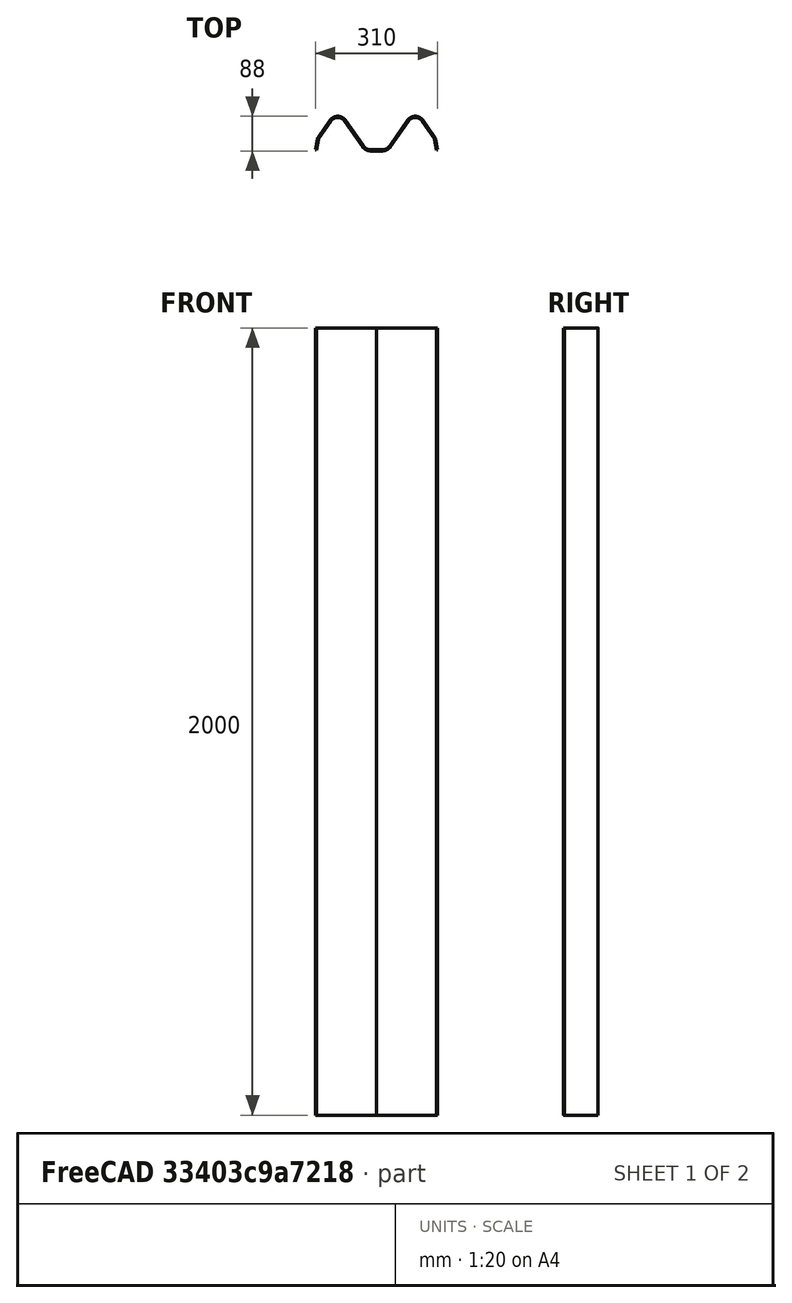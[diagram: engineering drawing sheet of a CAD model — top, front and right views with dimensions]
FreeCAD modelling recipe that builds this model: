
FCSTD DOCUMENT  (FreeCAD 0.21R33694 (Git))
Label: barrier
License: All rights reserved
LicenseURL: http://en.wikipedia.org/wiki/All_rights_reserved
objects: Sketcher::SketchObject×2, Fem::ConstraintFixed×2, Fem::ConstraintForce×2, Part::Offset2D×2, Fem::FemSolverObjectPython×1, App::MaterialObjectPython×1, Part::Mirroring×1, Part::FeaturePython×1, Part::Extrusion×1, Fem::FemMeshObjectPython×1, Fem::FemAnalysis×1
note: 7 computed .brp shape members not serialized (recipe doc carries the construction recipe); baked Part::Feature solids carry a one-line shape summary decoded from their .brp

FEATURE [Sketcher::SketchObject] Sketch
  FullyConstrained = false
  sketch-geometry (9):
    g0: LineSegment StartX=-155 StartY=0 StartZ=0 EndX=-150.163 EndY=27.4344 EndZ=0
    g1: ArcOfCircle CenterX=-140.315 CenterY=25.6979 CenterZ=0 NormalX=0 NormalY=0 NormalZ=1 AngleXU=0 Radius=10 StartAngle=2.53073 EndAngle=2.96706
    g2: LineSegment StartX=-148.506 StartY=31.4337 StartZ=0 EndX=-118.165 EndY=74.7658 EndZ=0
    g3: LineSegment StartX=0 StartY=0 StartZ=0 EndX=-14 EndY=0 EndZ=0
    g4: ArcOfCircle CenterX=-14 CenterY=24 CenterZ=0 NormalX=0 NormalY=0 NormalZ=1 AngleXU=0 Radius=24 StartAngle=3.75246 EndAngle=4.71239
    g5: LineSegment StartX=-33.6596 StartY=10.2342 StartZ=0 EndX=-78.8452 EndY=74.7658 EndZ=0
    g6: ArcOfCircle CenterX=-98.5049 CenterY=61 CenterZ=0 NormalX=0 NormalY=0 NormalZ=1 AngleXU=0 Radius=24 StartAngle=0.610865 EndAngle=2.53073
    g7: LineSegment StartX=-130.459 StartY=85 StartZ=0 EndX=-64.5536 EndY=85 EndZ=0
    g8: LineSegment StartX=-148.506 StartY=31.4337 StartZ=0 EndX=-148.506 EndY=74.2838 EndZ=0
  constraints (22):
    c: PointOnObject(g0,g-1)
    c: Angle(g0,g-2) = 0.174533
    c: Coincident(g3,g-1)
    c: PointOnObject(g3,g-1)
    c: Radius(g1) = 10
    c: DistanceX(g0,g3) = 155
    c: Radius(g4) = 24
    c: Angle(g-1,g5) = 2.18166
    c: DistanceX(g3,g3) = 14
    c: Horizontal(g7)
    c: DistanceY(g3,g7) = 85
    c: Tangent(g6,g7)
    c: Radius(g6) = 24
    c: Tangent(g6,g2) = 1.5708
    c: Tangent(g6,g5) = -1.5708
    c: Tangent(g1,g0) = 1.5708
    c: Tangent(g1,g2) = 1.5708
    c: Tangent(g4,g3) = 1.5708
    c: Tangent(g4,g5) = 1.5708
    c: Coincident(g8,g1)
    c: Vertical(g8)
    c: Angle(g2,g8) = 0.610865
FEATURE [Fem::ConstraintFixed] ConstraintFixed
  NormalDirection = (0,0,1)
FEATURE [Fem::ConstraintForce] ConstraintForce
  DirectionVector = (0.984808,-0.173648,0)
  Force = 15000
  NormalDirection = (-0.984808,0.173648,0)
  Reversed = true
FEATURE [Fem::FemSolverObjectPython] SolverCcxTools  # FEM object (typed FeaturePython)
  AnalysisType = 0
  BeamShellResultOutput3D = false
  BucklingFactors = 1
  EigenmodeHighLimit = 1000000
  EigenmodeLowLimit = 0
  EigenmodesCount = 10
  GeometricalNonlinearity = 0
  IterationsControlParameterCutb = 0.25,0.5,0.75,0.85,,,1.5,
  IterationsControlParameterIter = 4,8,9,200,10,400,,200,,
  IterationsControlParameterTimeUse = false
  IterationsThermoMechMaximum = 2000
  IterationsUserDefinedIncrementations = false
  IterationsUserDefinedTimeStepLength = false
  MaterialNonlinearity = 0
  MatrixSolverType = 0
  SplitInputWriter = false
  ThermoMechSteadyState = true
  TimeEnd = 1
  TimeInitialStep = 0.01
FEATURE [App::MaterialObjectPython] MaterialSolid  # material (typed FeaturePython)
  Category = 0
  Material = AuthorAndLicense=(c) 2014 M. Münch - GNU Lesser General Public License (LGPL),CardName=Steel-St-E-315,Density=7800 kg/m^3,Father=Metal,+13 more (map truncated)
FEATURE [Part::Offset2D] Offset2D
  Fill = true
  Intersection = false
  Join = 0
  Mode = 0
  SelfIntersection = false
  Source = -> Sketch
  Value = 3
FEATURE [Part::Mirroring] Part__Mirroring  label="Offset2D (Mirror #1)"
  Base = (0,0,0)
  Normal = (1,0,0)
  Source = -> Offset2D
FEATURE [Sketcher::SketchObject] Sketch001
  FullyConstrained = false
  sketch-geometry (8):
    g0: LineSegment StartX=-155 StartY=0 StartZ=0 EndX=-150.163 EndY=27.4344 EndZ=0
    g1: ArcOfCircle CenterX=-140.315 CenterY=25.6979 CenterZ=0 NormalX=0 NormalY=0 NormalZ=1 AngleXU=0 Radius=10 StartAngle=2.53073 EndAngle=2.96706
    g2: LineSegment StartX=-148.506 StartY=31.4337 StartZ=0 EndX=-118.165 EndY=74.7658 EndZ=0
    g3: LineSegment StartX=0 StartY=0 StartZ=0 EndX=-14 EndY=0 EndZ=0
    g4: ArcOfCircle CenterX=-14 CenterY=24 CenterZ=0 NormalX=0 NormalY=0 NormalZ=1 AngleXU=0 Radius=24 StartAngle=3.75246 EndAngle=4.71239
    g5: LineSegment StartX=-33.6596 StartY=10.2342 StartZ=0 EndX=-78.8452 EndY=74.7658 EndZ=0
    g6: ArcOfCircle CenterX=-98.5049 CenterY=61 CenterZ=0 NormalX=0 NormalY=0 NormalZ=1 AngleXU=0 Radius=24 StartAngle=0.610865 EndAngle=2.53073
    g7: LineSegment StartX=-143.773 StartY=85 StartZ=0 EndX=-53.9703 EndY=85 EndZ=0
  constraints (20):
    c: PointOnObject(g0,g-1)
    c: Angle(g0,g-2) = 0.174533
    c: Coincident(g3,g-1)
    c: PointOnObject(g3,g-1)
    c: Radius(g1) = 10
    c: DistanceX(g0,g3) = 155
    c: Radius(g4) = 24
    c: Angle(g-1,g5) = 2.18166
    c: Angle(g2,g-2) = 0.610865
    c: DistanceX(g3,g3) = 14
    c: Horizontal(g7)
    c: DistanceY(g3,g7) = 85
    c: Tangent(g6,g7)
    c: Radius(g6) = 24
    c: Tangent(g6,g2) = 1.5708
    c: Tangent(g6,g5) = -1.5708
    c: Tangent(g1,g0) = 1.5708
    c: Tangent(g1,g2) = 1.5708
    c: Tangent(g4,g3) = 1.5708
    c: Tangent(g4,g5) = 1.5708
FEATURE [Part::Offset2D] Offset2D001
  Fill = true
  Intersection = false
  Join = 0
  Mode = 0
  SelfIntersection = false
  Source = -> Sketch001
  Value = 3
FEATURE [Part::FeaturePython] BooleanFragments  # WARN: FeaturePython — macro-defined, semantics opaque (R4)
  Mode = 0
  Objects = -> [Part__Mirroring,Offset2D001]
  Tolerance = 0
FEATURE [Part::Extrusion] Extrude
  Base = -> BooleanFragments
  Dir = (0,0,1)
  DirMode = 2
  FaceMakerClass = Part::FaceMakerBullseye
  LengthFwd = 2000
  LengthRev = 0
  Solid = false
  Symmetric = false
FEATURE [Fem::FemMeshObjectPython] FEMMeshGmsh  # FEM object (typed FeaturePython)
  Algorithm2D = 0
  Algorithm3D = 0
  CharacteristicLengthMax = 50
  CharacteristicLengthMin = 0
  CoherenceMesh = true
  ElementDimension = 0
  ElementOrder = 1
  GeometryTolerance = 1e-06
  GroupsOfNodes = false
  HighOrderOptimize = 0
  MeshSizeFromCurvature = 12
  OptimizeNetgen = false
  OptimizeStd = true
  Part = -> Extrude
  RecombinationAlgorithm = 0
  Recombine3DAll = false
  RecombineAll = false
  SecondOrderLinear = false
FEATURE [Fem::ConstraintFixed] ConstraintFixed001
  NormalDirection = (0,0,1)
  Normals = (4) [(0,0,1),(0,0,-1),(0,0,1),(0,0,1)]
  Points = (4) [(0,-3,0),(0,-3,0),(0,-3,2000),(0,-3,2000)]
  References = -> [Offset2D,Extrude]
  Scale = 11
FEATURE [Fem::ConstraintForce] ConstraintForce001
  DirectionVector = (-1e-16,-1,0)
  Force = 15000
  NormalDirection = (1e-16,1,0)
  Points = (56) [(-78.8452,74.7658,2000),(-90.9558,83.7818,2000),(-106.054,83.7818,2000),(-118.165,74.7658,2000),(-78.8452,74.7658,1666.67),(-90.9558,83.7818,1666.67),+50 more]
  References = -> [Extrude]
  Reversed = true
  Scale = 33
FEATURE [Fem::FemAnalysis] Analysis
  Group = -> [ConstraintFixed,ConstraintForce,SolverCcxTools,MaterialSolid,ConstraintFixed001,ConstraintForce001]
